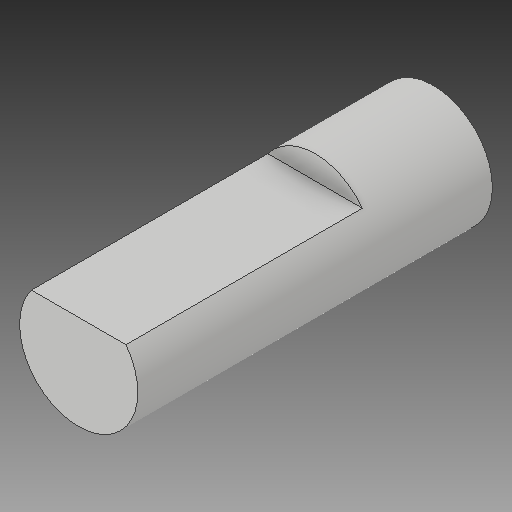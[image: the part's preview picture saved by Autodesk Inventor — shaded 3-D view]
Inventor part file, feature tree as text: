
AUTODESK INVENTOR PART (.ipt)
format: ipt  version: 2018 (Build 220112000, 112)  size: 98,304 bytes
history: native  units: mm
features: extrude x2, sketch x2, plane x1, projected_geometry x1
ambient origin geometry x8: Origin, YZ Plane, XZ Plane, XY Plane, X Axis, Y Axis, Z Axis, Center Point
bodies: Solid1 (feature_tree)
feature tree (6):
  extrude  "Extrusion1"  Depth=15.0mm TaperAngle=0.0deg
  plane  "Work Plane2"
  extrude  "Extrusion2"  Depth=10.0mm
  sketch  "Sketch1"  dims[d0=5.0mm d1=15.0mm d2=0.0mm]
  sketch  "Sketch2"  dims[d5=1.0mm d6=10.0mm d7=15.0mm d8=0.0mm]
  projected_geometry  "Projected Loop1"
